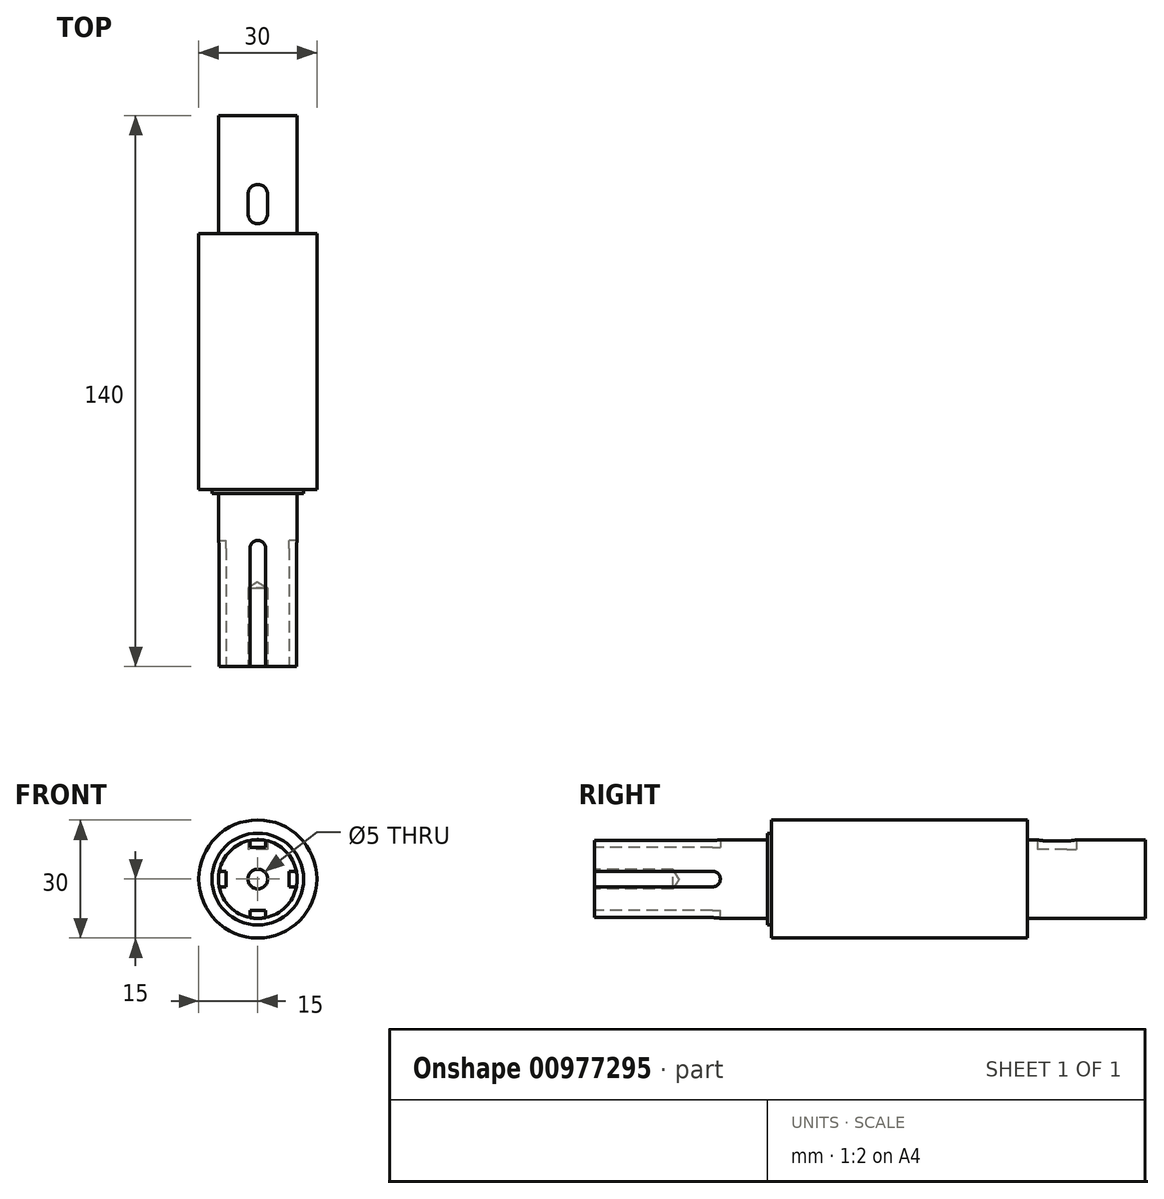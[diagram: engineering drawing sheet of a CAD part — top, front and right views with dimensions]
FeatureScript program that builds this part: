
annotation { "Feature Type Name" : "Feature", "Feature Type Description" : "" }
export const myFeature = defineFeature(function(context is Context, id is Id, definition is map)
    precondition{}
    {
        {
            var Q0;
            Q0=qCreatedBy(makeId("Front.planeOp"),FACE);
            var sketch = newSketch(context, id + "F0", { "sketchPlane" : qUnion([Q0])});
            skCircle(sketch, "E0", {"center": v(0, 0) * mm, "radius": 15 * mm});
            skCircle(sketch, "E1", {"center": v(0, 0) * mm, "radius": 10 * mm});
            skSolve(sketch);
        }
        {
            var Q0;
            Q0=makeQuery(id+"F0.imprint","IMPRINT",FACE,{"disambiguationData":[TD([[makeQuery(id+"F0.imprint","IMPRINT",EDGE,{"derivedFrom":sQuery(id+"F0.wireOp",EDGE,"E1")}),1.0]])]});
            extrude(context, id + "F1", {"entities" : qUnion([Q0]), "depth" : 45 * mm, "offsetDistance" : 25 * mm, "hasSecondDirection" : true, "secondDirectionOppositeDirection" : true, "secondDirectionDepth" : 95 * mm});
        }
        {
            var Q0;
            Q0=makeQuery(id+"F0.imprint","IMPRINT",FACE,{"disambiguationData":[TD([[makeQuery(id+"F0.imprint","IMPRINT",EDGE,{"derivedFrom":sQuery(id+"F0.wireOp",EDGE,"E0")}),1.0]])]});
            extrude(context, id + "F2", {"entities" : qUnion([Q0]), "operationType" : NewBodyOperationType.ADD, "oppositeDirection" : true, "depth" : 65 * mm, "offsetDistance" : 25 * mm});
        }
        {
            var Q0;
            Q0=qCreatedBy(makeId("Top.planeOp"),FACE);
            var sketch = newSketch(context, id + "F3", { "sketchPlane" : qUnion([Q0])});
            skLineSegment(sketch, "E2.bottom", {"start": v(-2.5, 75) * mm, "end": v(2.5, 75) * mm});
            skLineSegment(sketch, "E2.top", {"start": v(-2.5, 70) * mm, "end": v(2.5, 70) * mm});
            skLineSegment(sketch, "E2.left", {"start": v(-2.5, 75) * mm, "end": v(-2.5, 70) * mm});
            skLineSegment(sketch, "E2.right", {"start": v(2.5, 75) * mm, "end": v(2.5, 70) * mm});
            skPoint(sketch, "E2.middle", {"position": v(0, 72.5) * mm});
            skCircle(sketch, "E3", {"center": v(0, 75) * mm, "radius": 2.5 * mm});
            skCircle(sketch, "E4", {"center": v(0, 70) * mm, "radius": 2.5 * mm});
            skSolve(sketch);
        }
        {
            var Q0;
            Q0=qSketchRegion(id+"F3",true);
            extrude(context, id + "F4", {"entities" : qUnion([Q0]), "operationType" : NewBodyOperationType.REMOVE, "depth" : 25 * mm, "offsetDistance" : 25 * mm, "hasSecondDirection" : true, "secondDirectionOppositeDirection" : false, "secondDirectionDepth" : 7.5 * mm});
        }
        {
            var Q0;
            Q0=makeQuery(id+"F1.opExtrude","CAP_FACE",FACE,{"disambiguationData":[OSD([sQuery(id+"F0.wireOp",EDGE,"E1")])],"isStart":false});
            var sketch = newSketch(context, id + "F5", { "sketchPlane" : qUnion([Q0])});
            skCircle(sketch, "E5", {"center": v(0, 0) * mm, "radius": 10 * mm});
            skLineSegment(sketch, "E6.bottom", {"start": v(-2, 12.5) * mm, "end": v(2, 12.5) * mm});
            skLineSegment(sketch, "E6.top", {"start": v(-2, -12.5) * mm, "end": v(2, -12.5) * mm});
            skLineSegment(sketch, "E6.left", {"start": v(-2, 12.5) * mm, "end": v(-2, -12.5) * mm});
            skLineSegment(sketch, "E6.right", {"start": v(2, 12.5) * mm, "end": v(2, -12.5) * mm});
            skLineSegment(sketch, "E7.bottom", {"start": v(12.5, -2) * mm, "end": v(-12.5, -2) * mm});
            skLineSegment(sketch, "E7.top", {"start": v(12.5, 2) * mm, "end": v(-12.5, 2) * mm});
            skLineSegment(sketch, "E7.left", {"start": v(12.5, -2) * mm, "end": v(12.5, 2) * mm});
            skLineSegment(sketch, "E7.right", {"start": v(-12.5, -2) * mm, "end": v(-12.5, 2) * mm});
            skLineSegment(sketch, "E8.bottom", {"start": v(-2, 8) * mm, "end": v(2, 8) * mm});
            skLineSegment(sketch, "E8.top", {"start": v(-2, -8) * mm, "end": v(2, -8) * mm});
            skLineSegment(sketch, "E8.left", {"start": v(-2, 8) * mm, "end": v(-2, -8) * mm});
            skLineSegment(sketch, "E8.right", {"start": v(2, 8) * mm, "end": v(2, -8) * mm});
            skLineSegment(sketch, "E9.bottom", {"start": v(8, 2) * mm, "end": v(-8, 2) * mm});
            skLineSegment(sketch, "E9.top", {"start": v(8, -2) * mm, "end": v(-8, -2) * mm});
            skLineSegment(sketch, "E9.left", {"start": v(8, 2) * mm, "end": v(8, -2) * mm});
            skLineSegment(sketch, "E9.right", {"start": v(-8, 2) * mm, "end": v(-8, -2) * mm});
            skSolve(sketch);
        }
        {
            var Q0;
            {var subQ5=sQuery(id+"F5.wireOp",EDGE,"E8.bottom");Q0=makeQuery(id+"F5.imprint","IMPRINT",FACE,{"disambiguationData":[TD([[makeQuery(id+"F5.imprint","IMPRINT",EDGE,{"derivedFrom":subQ5}),1.0]])]});}
            var Q1;
            {var subQ5=sQuery(id+"F5.wireOp",EDGE,"E9.left");Q1=makeQuery(id+"F5.imprint","IMPRINT",FACE,{"disambiguationData":[TD([[makeQuery(id+"F5.imprint","IMPRINT",EDGE,{"derivedFrom":subQ5}),1.0]])]});}
            var Q2;
            {var subQ5=sQuery(id+"F5.wireOp",EDGE,"E8.top");Q2=makeQuery(id+"F5.imprint","IMPRINT",FACE,{"disambiguationData":[TD([[makeQuery(id+"F5.imprint","IMPRINT",EDGE,{"derivedFrom":subQ5}),-1.0]])]});}
            var Q3;
            {var subQ5=sQuery(id+"F5.wireOp",EDGE,"E9.right");Q3=makeQuery(id+"F5.imprint","IMPRINT",FACE,{"disambiguationData":[TD([[makeQuery(id+"F5.imprint","IMPRINT",EDGE,{"derivedFrom":subQ5}),-1.0]])]});}
            extrude(context, id + "F6", {"entities" : qUnion([Q0, Q1, Q2, Q3]), "operationType" : NewBodyOperationType.REMOVE, "oppositeDirection" : true, "depth" : 30 * mm, "offsetDistance" : 25 * mm});
        }
        {
            var Q0;
            Q0=makeQuery(id+"F6.boolean.opBoolean","COPY",FACE,{"derivedFrom":makeQuery(id+"F6.opExtrude","SWEPT_FACE",FACE,{"disambiguationData":[OSD([sQuery(id+"F5.wireOp",EDGE,"E8.bottom")])]})});
            var sketch = newSketch(context, id + "F7", { "sketchPlane" : qUnion([Q0])});
            skCircle(sketch, "E10", {"center": v(0, -15) * mm, "radius": 2 * mm});
            skSolve(sketch);
        }
        {
            var Q0;
            Q0=qSketchRegion(id+"F7",true);
            extrude(context, id + "F8", {"entities" : qUnion([Q0]), "operationType" : NewBodyOperationType.REMOVE, "depth" : 25 * mm, "offsetDistance" : 25 * mm});
        }
        {
            var Q0;
            Q0=makeQuery(id+"F6.boolean.opBoolean","COPY",FACE,{"derivedFrom":makeQuery(id+"F6.opExtrude","SWEPT_FACE",FACE,{"disambiguationData":[OSD([sQuery(id+"F5.wireOp",EDGE,"E9.left")])]})});
            var sketch = newSketch(context, id + "F9", { "sketchPlane" : qUnion([Q0])});
            skCircle(sketch, "E11", {"center": v(-15, 0) * mm, "radius": 2 * mm});
            skSolve(sketch);
        }
        {
            var Q0;
            Q0=qSketchRegion(id+"F9",true);
            extrude(context, id + "F10", {"entities" : qUnion([Q0]), "operationType" : NewBodyOperationType.REMOVE, "depth" : 25 * mm, "offsetDistance" : 25 * mm});
        }
        {
            var Q0;
            Q0=makeQuery(id+"F6.boolean.opBoolean","COPY",FACE,{"derivedFrom":makeQuery(id+"F6.opExtrude","SWEPT_FACE",FACE,{"disambiguationData":[OSD([sQuery(id+"F5.wireOp",EDGE,"E8.top")])]})});
            var sketch = newSketch(context, id + "F11", { "sketchPlane" : qUnion([Q0])});
            skCircle(sketch, "E12", {"center": v(0, 15) * mm, "radius": 2 * mm});
            skSolve(sketch);
        }
        {
            var Q0;
            Q0=qSketchRegion(id+"F11",true);
            extrude(context, id + "F12", {"entities" : qUnion([Q0]), "operationType" : NewBodyOperationType.REMOVE, "depth" : 25 * mm, "offsetDistance" : 25 * mm});
        }
        {
            var Q0;
            Q0=makeQuery(id+"F6.boolean.opBoolean","COPY",FACE,{"derivedFrom":makeQuery(id+"F6.opExtrude","SWEPT_FACE",FACE,{"disambiguationData":[OSD([sQuery(id+"F5.wireOp",EDGE,"E9.right")])]})});
            var sketch = newSketch(context, id + "F13", { "sketchPlane" : qUnion([Q0])});
            skCircle(sketch, "E13", {"center": v(15, 0) * mm, "radius": 2 * mm});
            skSolve(sketch);
        }
        {
            var Q0;
            Q0=qSketchRegion(id+"F13",true);
            extrude(context, id + "F14", {"entities" : qUnion([Q0]), "operationType" : NewBodyOperationType.REMOVE, "depth" : 25 * mm, "offsetDistance" : 25 * mm});
        }
        {
            var Q0;
            Q0=makeQuery(id+"F1.opExtrude","CAP_FACE",FACE,{"disambiguationData":[OSD([sQuery(id+"F0.wireOp",EDGE,"E1")])],"isStart":false});
            var sketch = newSketch(context, id + "F15", { "sketchPlane" : qUnion([Q0])});
            skPoint(sketch, "E14", {"position": v(0, 0) * mm});
            skSolve(sketch);
        }
        {
            var Q0;
            Q0=sQuery(id+"F15.wireOp",VERTEX,"E14");
            var Q1;
            Q1=makeQuery(id+"F1.opExtrude","SWEPT_BODY",BODY,{"disambiguationData":[OSD([sQuery(id+"F0.wireOp",EDGE,"E1")])]});
            hole(context, id + "F16", {"style" : HoleStyle.SIMPLE, "endStyle" : HoleEndStyle.BLIND, "holeDiameter" : 5 * mm, "majorDiameter" : 5 * mm, "holeDepth" : 20 * mm, "isTappedThrough" : true, "tappedDepth" : 12 * mm, "tapClearance" : 3, "locations" : qUnion([Q0]), "scope" : qUnion([Q1])});
        }
        {
            var Q0;
            Q0=makeQuery(id+"F0.imprint","IMPRINT",FACE,{"disambiguationData":[TD([[makeQuery(id+"F0.imprint","IMPRINT",EDGE,{"derivedFrom":sQuery(id+"F0.wireOp",EDGE,"E0")}),1.0]])]});
            var sketch = newSketch(context, id + "F17", { "sketchPlane" : qUnion([Q0])});
            skCircle(sketch, "E15", {"center": v(0, 0) * mm, "radius": 11.65 * mm});
            skSolve(sketch);
        }
        {
            var Q0;
            Q0=qSketchRegion(id+"F17",true);
            extrude(context, id + "F18", {"entities" : qUnion([Q0]), "operationType" : NewBodyOperationType.ADD, "depth" : 1 * mm, "offsetDistance" : 25 * mm});
        }
    });
